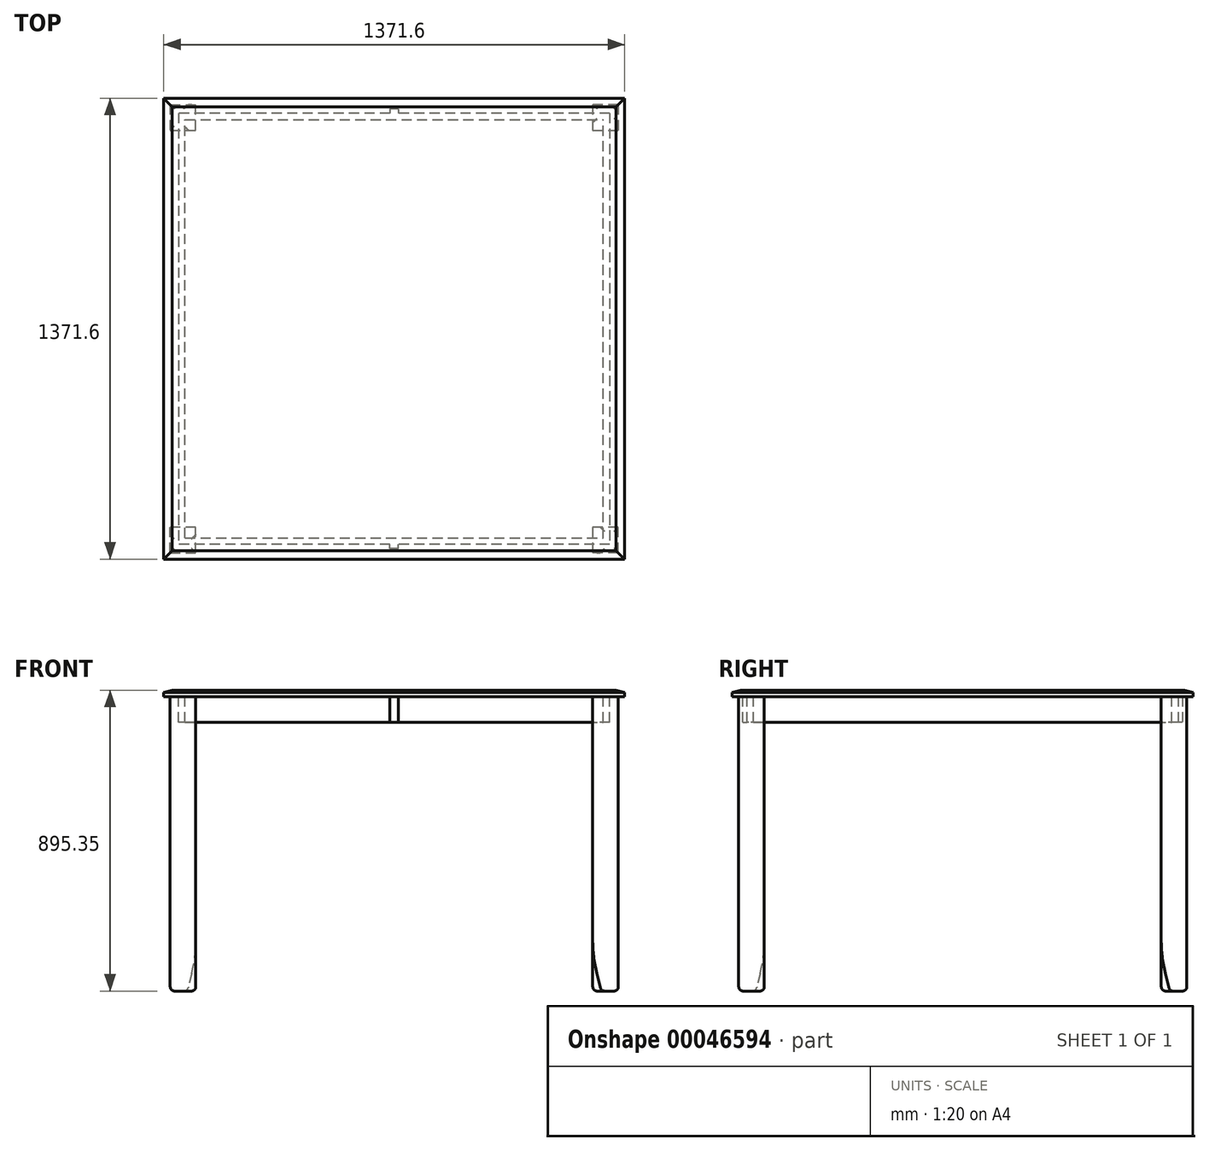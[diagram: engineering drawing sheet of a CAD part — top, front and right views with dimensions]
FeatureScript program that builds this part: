
annotation { "Feature Type Name" : "Feature", "Feature Type Description" : "" }
export const myFeature = defineFeature(function(context is Context, id is Id, definition is map)
    precondition{}
    {
        {
            var Q0;
            Q0=qCreatedBy(makeId("Top.planeOp"),FACE);
            var sketch = newSketch(context, id + "F0", { "sketchPlane" : qUnion([Q0])});
            skLineSegment(sketch, "E0.rect.bottom", {"start": v(685.8, 685.8) * mm, "end": v(-685.8, 685.8) * mm});
            skLineSegment(sketch, "E0.rect.top", {"start": v(685.8, -685.8) * mm, "end": v(-685.8, -685.8) * mm});
            skLineSegment(sketch, "E0.rect.left", {"start": v(685.8, 685.8) * mm, "end": v(685.8, -685.8) * mm});
            skLineSegment(sketch, "E0.rect.right", {"start": v(-685.8, 685.8) * mm, "end": v(-685.8, -685.8) * mm});
            skPoint(sketch, "E0.rect.middle", {"position": v(0, 0) * mm});
            skSolve(sketch);
        }
        {
            var Q0;
            Q0 = qSketchRegion(id + "F0", true);
            extrude(context, id + "F1", {"entities" : qUnion([Q0]), "oppositeDirection" : true, "depth" : 19.05 * mm});
        }
        {
            var Q0;
            Q0=makeQuery(id+"F1.opExtrude","CAP_FACE",FACE,{"disambiguationData":[OSD([sQuery(id+"F0.wireOp",EDGE,"E0.rect.bottom"),sQuery(id+"F0.wireOp",EDGE,"E0.rect.top"),sQuery(id+"F0.wireOp",EDGE,"E0.rect.left"),sQuery(id+"F0.wireOp",EDGE,"E0.rect.right")])],"isStart":false});
            var sketch = newSketch(context, id + "F2", { "sketchPlane" : qUnion([Q0])});
            skLineSegment(sketch, "E1.rect.bottom", {"start": v(641.35, -641.35) * mm, "end": v(-641.35, -641.35) * mm});
            skLineSegment(sketch, "E1.rect.top", {"start": v(641.35, 641.35) * mm, "end": v(-641.35, 641.35) * mm});
            skLineSegment(sketch, "E1.rect.left", {"start": v(641.35, -641.35) * mm, "end": v(641.35, 641.35) * mm});
            skLineSegment(sketch, "E1.rect.right", {"start": v(-641.35, -641.35) * mm, "end": v(-641.35, 641.35) * mm});
            skPoint(sketch, "E1.rect.middle", {"position": v(0, 0) * mm});
            skLineSegment(sketch, "E2.rect.bottom", {"start": v(-622.3, 622.3) * mm, "end": v(622.3, 622.3) * mm});
            skLineSegment(sketch, "E2.rect.top", {"start": v(-622.3, -622.3) * mm, "end": v(622.3, -622.3) * mm});
            skLineSegment(sketch, "E2.rect.left", {"start": v(-622.3, 622.3) * mm, "end": v(-622.3, -622.3) * mm});
            skLineSegment(sketch, "E2.rect.right", {"start": v(622.3, 622.3) * mm, "end": v(622.3, -622.3) * mm});
            skSolve(sketch);
        }
        {
            var Q0;
            Q0 = qSketchRegion(id + "F2", true);
            extrude(context, id + "F3", {"entities" : qUnion([Q0]), "operationType" : NewBodyOperationType.ADD, "depth" : 76.2 * mm});
        }
        {
            var Q0;
            {var subQ0=sQuery(id+"F0.wireOp",EDGE,"E0.rect.right");var subQ1=sQuery(id+"F0.wireOp",EDGE,"E0.rect.left");var subQ2=sQuery(id+"F0.wireOp",EDGE,"E0.rect.top");var subQ3=sQuery(id+"F0.wireOp",EDGE,"E0.rect.bottom");Q0=makeQuery(id+"F3.boolean.opBoolean","SPLIT",FACE,{"disambiguationData":[TD([makeQuery(id+"F1.opExtrude","SWEPT_FACE",FACE,{"disambiguationData":[OSD([subQ3])]})])],"derivedFrom":makeQuery(id+"F1.opExtrude","CAP_FACE",FACE,{"disambiguationData":[OSD([subQ3,subQ2,subQ1,subQ0])],"isStart":false})});}
            var sketch = newSketch(context, id + "F4", { "sketchPlane" : qUnion([Q0])});
            skLineSegment(sketch, "E3.bottom", {"start": v(-666.75, 666.75) * mm, "end": v(-590.55, 666.75) * mm});
            skLineSegment(sketch, "E3.top", {"start": v(-666.75, 590.55) * mm, "end": v(-590.55, 590.55) * mm});
            skLineSegment(sketch, "E3.left", {"start": v(-666.75, 666.75) * mm, "end": v(-666.75, 590.55) * mm});
            skLineSegment(sketch, "E3.right", {"start": v(-590.55, 666.75) * mm, "end": v(-590.55, 590.55) * mm});
            skSolve(sketch);
        }
        {
            var Q0;
            Q0 = qSketchRegion(id + "F4", true);
            extrude(context, id + "F5", {"entities" : qUnion([Q0]), "depth" : 876.3 * mm});
        }
        {
            var Q0;
            Q0=qCreatedBy(makeId("Front.planeOp"),FACE);
            var sketch = newSketch(context, id + "F6", { "sketchPlane" : qUnion([Q0])});
            skLineSegment(sketch, "E4", {"start": v(0, 0) * mm, "end": v(0, -525.56) * mm, "construction": true});
            skSolve(sketch);
        }
        {
            var Q0;
            Q0=makeQuery(id+"F10.opPattern","COPY",EDGE,{"derivedFrom":makeQuery(id+"F5.opExtrude","CAP_EDGE",EDGE,{"disambiguationData":[OSD([sQuery(id+"F4.wireOp",EDGE,"E3.right")])],"isStart":false}),"instanceName":"2"});
            var Q1;
            Q1=makeQuery(id+"F5.opExtrude","CAP_EDGE",EDGE,{"disambiguationData":[OSD([sQuery(id+"F4.wireOp",EDGE,"E3.top")])],"isStart":false});
            chamfer(context, id + "F7", {"entities" : qUnion([Q0, Q1]), "chamferType" : ChamferType.TWO_OFFSETS, "width1" : 25.4 * mm, "oppositeDirection" : false, "width2" : 101.6 * mm, "tangentPropagation" : true});
        }
        {
            var Q0;
            Q0=makeQuery(id+"F5.opExtrude","CAP_FACE",FACE,{"disambiguationData":[OSD([sQuery(id+"F4.wireOp",EDGE,"E3.bottom"),sQuery(id+"F4.wireOp",EDGE,"E3.top"),sQuery(id+"F4.wireOp",EDGE,"E3.left"),sQuery(id+"F4.wireOp",EDGE,"E3.right")])],"isStart":false});
            fillet(context, id + "F8", {"entities" : qUnion([Q0]), "radius" : 12.7 * mm, "tangentPropagation" : true, "allowEdgeOverflow" : false});
        }
        {
            var Q0;
            {var subQ0=sQuery(id+"F4.wireOp",EDGE,"E3.top");Q0=makeQuery(id+"F7.opChamfer","BLEND_EDGE",EDGE,{"blendedFrom":[makeQuery(id+"F5.opExtrude","CAP_EDGE",EDGE,{"disambiguationData":[OSD([subQ0])],"isStart":false}),makeQuery(id+"F5.opExtrude","SWEPT_FACE",FACE,{"disambiguationData":[OSD([subQ0])]})],"blendedInto":[makeQuery(id+"F5.opExtrude","SWEPT_FACE",FACE,{"disambiguationData":[OSD([subQ0])]})]});}
            fillet(context, id + "F9", {"entities" : qUnion([Q0]), "radius" : 406.4 * mm, "tangentPropagation" : true, "allowEdgeOverflow" : false});
        }
        {
            var Q0;
            Q0=makeQuery(id+"F5.opExtrude","SWEPT_BODY",BODY,{"disambiguationData":[OSD([sQuery(id+"F4.wireOp",EDGE,"E3.bottom"),sQuery(id+"F4.wireOp",EDGE,"E3.top"),sQuery(id+"F4.wireOp",EDGE,"E3.left"),sQuery(id+"F4.wireOp",EDGE,"E3.right")])]});
            var Q1;
            Q1=sQuery(id+"F6.wireOp",EDGE,"E4");
            circularPattern(context, id + "F10", {"entities" : qUnion([Q0]), "axis" : qUnion([Q1]), "angle" : 360 * degree, "instanceCount" : 4, "equalSpace" : true});
        }
        {
            var Q0;
            Q0=makeQuery(id+"F1.opExtrude","CAP_FACE",FACE,{"disambiguationData":[OSD([sQuery(id+"F0.wireOp",EDGE,"E0.rect.bottom"),sQuery(id+"F0.wireOp",EDGE,"E0.rect.top"),sQuery(id+"F0.wireOp",EDGE,"E0.rect.left"),sQuery(id+"F0.wireOp",EDGE,"E0.rect.right")])],"isStart":true});
            chamfer(context, id + "F11", {"entities" : qUnion([Q0]), "chamferType" : ChamferType.TWO_OFFSETS, "width1" : 6.35 * mm, "oppositeDirection" : true, "width2" : 25.4 * mm, "tangentPropagation" : true});
        }
        {
            var Q0;
            Q0=makeQuery(id+"F3.opExtrude","SWEPT_FACE",FACE,{"disambiguationData":[OSD([sQuery(id+"F2.wireOp",EDGE,"E1.rect.top")])]});
            var sketch = newSketch(context, id + "F12", { "sketchPlane" : qUnion([Q0])});
            skLineSegment(sketch, "E5.bottom", {"start": v(-12.7, -95.25) * mm, "end": v(12.7, -95.25) * mm});
            skLineSegment(sketch, "E5.top", {"start": v(-12.7, -19.05) * mm, "end": v(12.7, -19.05) * mm});
            skLineSegment(sketch, "E5.left", {"start": v(-12.7, -95.25) * mm, "end": v(-12.7, -19.05) * mm});
            skLineSegment(sketch, "E5.right", {"start": v(12.7, -95.25) * mm, "end": v(12.7, -19.05) * mm});
            skLineSegment(sketch, "E6", {"start": v(0, 0) * mm, "end": v(0, -95.25) * mm, "construction": true});
            skPoint(sketch, "E6.startSnap0", {"position": v(0, -19.05) * mm});
            skSolve(sketch);
        }
        {
            var Q0;
            Q0=makeQuery(id+"F12.imprint","IMPRINT",FACE,{"disambiguationData":[TD([[makeQuery(id+"F12.imprint","IMPRINT",EDGE,{"derivedFrom":sQuery(id+"F12.wireOp",EDGE,"E5.bottom")}),-1.0]])]});
            extrude(context, id + "F13", {"entities" : qUnion([Q0]), "operationType" : NewBodyOperationType.ADD, "depth" : 12.7 * mm});
        }
        {
            var Q0;
            Q0=makeQuery(id+"F3.opExtrude","SWEPT_FACE",FACE,{"disambiguationData":[OSD([sQuery(id+"F2.wireOp",EDGE,"E1.rect.bottom")])]});
            var sketch = newSketch(context, id + "F14", { "sketchPlane" : qUnion([Q0])});
            skLineSegment(sketch, "E7.bottom", {"start": v(-12.7, -19.05) * mm, "end": v(12.7, -19.05) * mm});
            skLineSegment(sketch, "E7.top", {"start": v(-12.7, -95.25) * mm, "end": v(12.7, -95.25) * mm});
            skLineSegment(sketch, "E7.left", {"start": v(-12.7, -19.05) * mm, "end": v(-12.7, -95.25) * mm});
            skLineSegment(sketch, "E7.right", {"start": v(12.7, -19.05) * mm, "end": v(12.7, -95.25) * mm});
            skSolve(sketch);
        }
        {
            var Q0;
            Q0 = qSketchRegion(id + "F14", true);
            extrude(context, id + "F15", {"entities" : qUnion([Q0]), "operationType" : NewBodyOperationType.ADD, "depth" : 12.7 * mm});
        }
    });
